# Revit family: Bernhardt_Design-Tables-Conference-LaPaz
name_source: partatom
category: Furniture
revit_build: Autodesk Revit 2016 (Build: 20150714_1515(x64)
units: mm (PartAtom-declared; Revit-internal decimal feet)

## family parameters
Always vertical = Yes
Cut with Voids When Loaded = No
OmniClass Number = 23.40.20.00
OmniClass Title = General Furniture and Specialties
Room Calculation Point = No
Shared = No
Work Plane-Based = No

## types (14) — shared parameters
Manufacturer = Bernhardt Design
Model = La Paz
URL = http://www.bernhardtdesign.com

## per-type parameters (varying)
| type | Base Distance | Catalog | Rect Depth | Rect Inner Depth | Rect Inner Width | Rect Width | SKU |
| La Paz - 66" x 36" | 0.01 " | LPS-EFA | 18 " | 17.336 " | 32.336 " | 33 " | LPS-EFA |
| La Paz - 72" x 36" | 3.01 " | LPS-EGA | 18 " | 17.336 " | 35.336 " | 36 " | LPS-EGA |
| La Paz - 72" x 42" | 3.01 " | LPS-EGB | 21 " | 20.336 " | 35.336 " | 36 " | LPS-EGB |
| La Paz - 78" x 42" | 6.01 " | LPS-EHB | 21 " | 20.336 " | 38.336 " | 39 " | LPS-EHB |
| La Paz - 84" x 42" | 9.01 " | LPS-EIB | 21 " | 20.336 " | 41.336 " | 42 " | LPS-EIB |
| La Paz - 90" x 42" | 12.01 " | LPS-EJC | 21 " | 20.336 " | 44.336 " | 45 " | LPS-EJC |
| La Paz - 96" x 42" | 15.01 " | LPS-EKB | 21 " | 20.336 " | 47.336 " | 48 " | LPS-EKB |
| La Paz - 102" x 42" | 18.01 " | LPS-ELB | 21 " | 20.336 " | 50.336 " | 51 " | LPS-ELB |
| La Paz - 108" x 42" | 21.01 " | LPS-EMB | 21 " | 20.336 " | 53.336 " | 54 " | LPS-EMB |
| La Paz - 84" x 48" | 9.01 " | LPS-EIC | 24 " | 23.336 " | 41.336 " | 42 " | LPS-EIC |
| La Paz - 90" x 48" | 12.01 " | LPS-EJC | 24 " | 23.336 " | 44.336 " | 45 " | LPS-EJC |
| La Paz - 96" x 48" | 15.01 " | LPS-EKC | 24 " | 23.336 " | 47.336 " | 48 " | LPS-EKC |
| La Paz - 102" x 48" | 18.01 " | LPS-ELC | 24 " | 23.336 " | 50.336 " | 51 " | LPS-ELC |
| La Paz - 108" x 48" | 21.01 " | LPS-EMC | 24 " | 23.336 " | 53.336 " | 54 " | LPS-EMC |

## geometry (parser evidence)
native form markers: Sweep x6
no freeform markers — native parametric forms only
